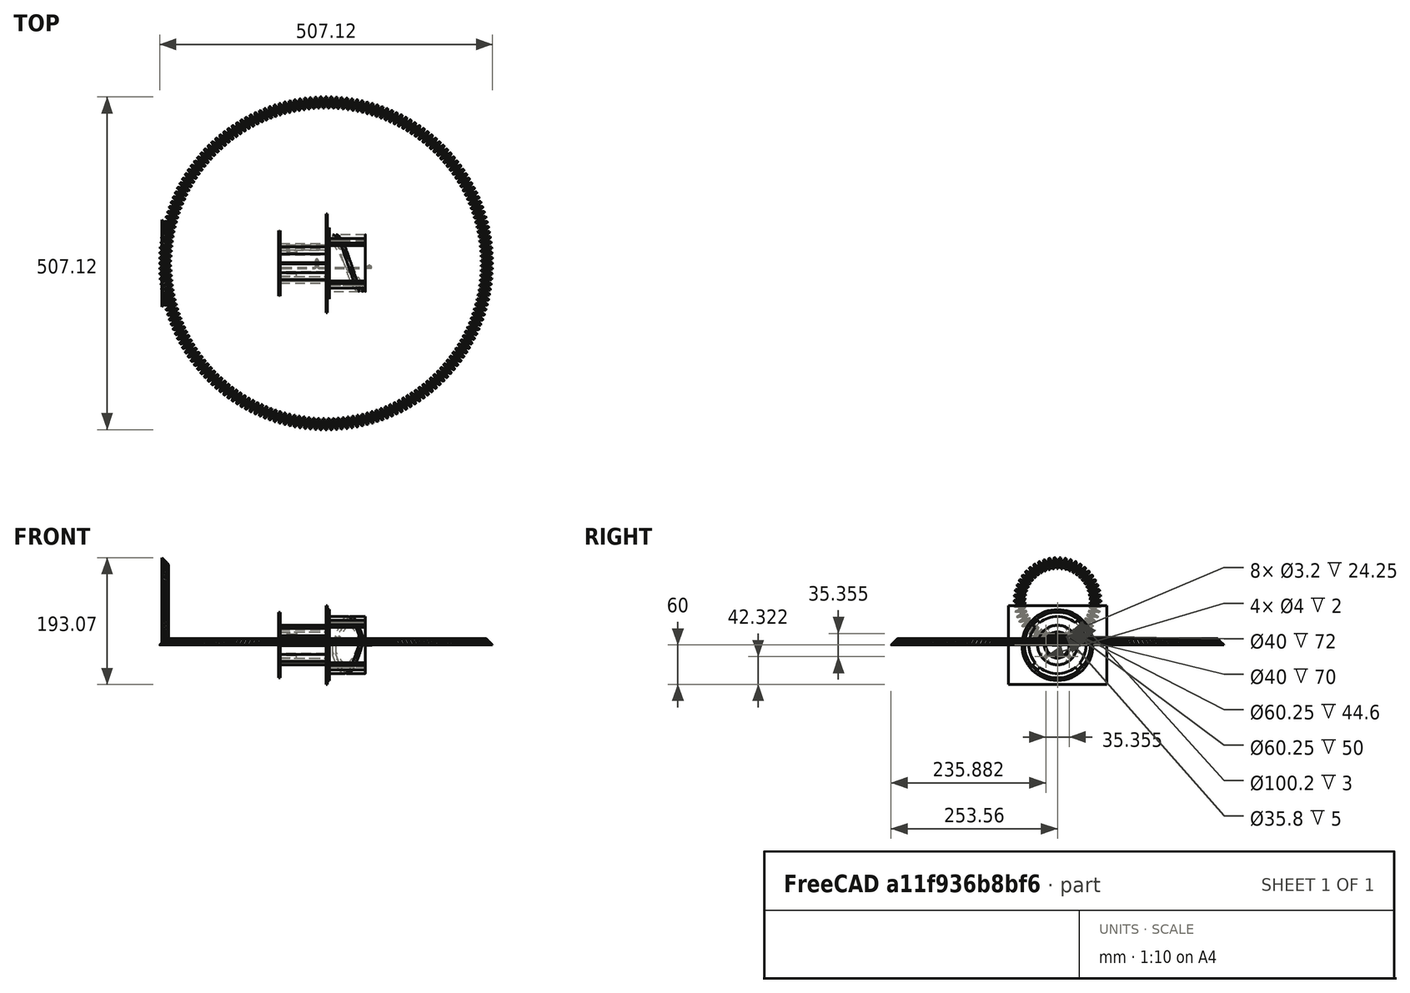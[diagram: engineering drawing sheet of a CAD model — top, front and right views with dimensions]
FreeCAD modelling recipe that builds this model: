
FCSTD DOCUMENT  (FreeCAD 1.0R38641 +468 (Git))
Label: knitting_machine
License: All rights reserved
LicenseURL: https://en.wikipedia.org/wiki/All_rights_reserved
objects: Sketcher::SketchObject×18, PartDesign::Pad×9, App::FeaturePython×6, PartDesign::Body×5, App::Link×5, App::Part×4, PartDesign::PolarPattern×3, Part::FeaturePython×3, PartDesign::AdditivePipe×2, PartDesign::AdditiveLoft×2, PartDesign::Pocket×2, PartDesign::SubtractiveHelix×2, PartDesign::Groove×2, Spreadsheet::Sheet×1, Image::ImagePlane×1, PartDesign::Chamfer×1, Assembly::JointGroup×1, Assembly::AssemblyObject×1
note: 110 computed .brp shape members not serialized (recipe doc carries the construction recipe); baked Part::Feature solids carry a one-line shape summary decoded from their .brp

FEATURE [Spreadsheet::Sheet] Spreadsheet  label="MasterSpreadsheet"
  cells = A2='hole_diameter; B2(hole_diameter)==40 mm; A3='needle_number; B3(needle_number)=12; A4='needle_length; B4(needle_length)==13.8 cm; A5='needle_thickness; B5(needle_thickness)==1.9 mm; A6='needle_width; B6(needle_width)==1.2 mm; A7='needle_knob_protrusion; B7(needle_knob_protrusion)==12.5 mm; A8='needle_know_height; B8(needle_knob_height)==needle_thickness * 2 + 0.1 mm; A9='travel_dist; B9(travel_dist)==40 mm; A10='travel_angle; B10(travel_angle)==160 °; A11='baseplate_diameter; B11(baseplate_diameter)==100 mm; A12='gear_module; B12(gear_module)=2; A13='gear_pressure_angle; B13(gear_pressure_angle)==20 °; A14='driven_Z; B14(driven_Z)=36; A15='driven_PCD; B15(driven_PCD)=72; A16='gear_Ck; B16(gear_Ck)==250 mm
FEATURE [Image::ImagePlane] needle_1  label="needle-1"
  XSize = 140
  YSize = 18.51
FEATURE [Sketcher::SketchObject] Sketch  label="Needle_profile"
  ArcFitTolerance = 1e-06
  AttachmentSupport = -> [XY_Plane001]
  FullyConstrained = true
  MakeInternals = false
  MapMode = 5
  expr: Constraints[19] = <<MasterSpreadsheet>>.needle_thickness + 0.1 mm
  expr: Constraints[29] = <<MasterSpreadsheet>>.needle_knob_protrusion
  sketch-geometry (11):
    g0: LineSegment StartX=-67 StartY=-7 StartZ=0 EndX=-18.2 EndY=-7 EndZ=0
    g1: LineSegment StartX=-15 StartY=-3.8 StartZ=0 EndX=-15 EndY=4.55 EndZ=0
    g2: LineSegment StartX=-13.95 StartY=5.5 StartZ=0 EndX=-14.05 EndY=5.5 EndZ=0
    g3: LineSegment StartX=-13 StartY=4.55 StartZ=0 EndX=-13 EndY=-3.8 EndZ=0
    g4: LineSegment StartX=-9.8 StartY=-7 StartZ=0 EndX=60 EndY=-7 EndZ=0
    g5: ArcOfCircle CenterX=-18.2 CenterY=-3.8 CenterZ=0 NormalX=0 NormalY=0 NormalZ=1 AngleXU=0 Radius=3.2 StartAngle=4.71239 EndAngle=6.28319
    g6: GeomPoint [constr] X=-15 Y=-7 Z=0
    g7: ArcOfCircle CenterX=-9.8 CenterY=-3.8 CenterZ=0 NormalX=0 NormalY=0 NormalZ=1 AngleXU=0 Radius=3.2 StartAngle=3.14159 EndAngle=4.71239
    g8: GeomPoint [constr] X=-13 Y=-7 Z=0
    g9: ArcOfCircle CenterX=-14.05 CenterY=4.55 CenterZ=0 NormalX=0 NormalY=0 NormalZ=1 AngleXU=0 Radius=0.95 StartAngle=1.5708 EndAngle=3.14159
    g10: ArcOfCircle CenterX=-13.95 CenterY=4.55 CenterZ=0 NormalX=0 NormalY=0 NormalZ=1 AngleXU=0 Radius=0.95 StartAngle=3e-16 EndAngle=1.5708
  constraints (30):
    c: Horizontal(g0)
    c: Vertical(g1)
    c: Vertical(g3)
    c: Horizontal(g4)
    c: Horizontal(g8,g6)
    c: Horizontal(g2)
    c: PointOnObject(g6,g0)
    c: PointOnObject(g6,g1)
    c: Tangent(g0,g5) = -1.5708
    c: Tangent(g1,g5) = -1.5708
    c: PointOnObject(g8,g3)
    c: PointOnObject(g8,g4)
    c: Tangent(g3,g7) = -1.5708
    c: Tangent(g4,g7) = -1.5708
    c: Equal(g5,g7)
    c: Distance(g0,g-1) = 7
    c: Distance(g0,g-2) = 67
    c: DistanceX(g-1,g4) = 60
    c: Distance(g3,g-2) = 13
    c: DistanceX(g1,g3) = 2
    c: Horizontal(g1,g3)
    c: Radius(g7) = 3.2
    c: Distance(g2,g2) = 0.1
    c: Coincident(g9,g1)
    c: Horizontal(g9,g1)
    c: Tangent(g9,g2) = -1.5708
    c: Coincident(g10,g3)
    c: Horizontal(g10,g3)
    c: Tangent(g10,g2) = -1.5708
    c: DistanceY(g4,g2) = 12.5
FEATURE [Sketcher::SketchObject] Sketch001  label="Needle_section"
  ArcFitTolerance = 1e-06
  AttachmentSupport = -> [YZ_Plane001]
  ExternalGeometry = -> [Sketch]
  FullyConstrained = true
  MakeInternals = false
  MapMode = 5
  Placement = pos=(0,0,0) rot=(0.57735,0.57735,0.57735;2.0944rad)
  expr: Constraints[26] = <<MasterSpreadsheet>>.needle_thickness
  expr: Constraints[27] = <<MasterSpreadsheet>>.needle_width
  sketch-geometry (13):
    g0: LineSegment StartX=-7.95 StartY=0.1 StartZ=0 EndX=-7.95 EndY=-0.1 EndZ=0
    g1: LineSegment StartX=-7.45 StartY=-0.6 StartZ=0 EndX=-6.55 EndY=-0.6 EndZ=0
    g2: LineSegment StartX=-6.05 StartY=-0.1 StartZ=0 EndX=-6.05 EndY=0.1 EndZ=0
    g3: LineSegment StartX=-6.55 StartY=0.6 StartZ=0 EndX=-7.45 EndY=0.6 EndZ=0
    g4: ArcOfCircle CenterX=-7.45 CenterY=0.1 CenterZ=0 NormalX=0 NormalY=0 NormalZ=1 AngleXU=0 Radius=0.5 StartAngle=1.5708 EndAngle=3.14159
    g5: ArcOfCircle CenterX=-7.45 CenterY=-0.1 CenterZ=0 NormalX=0 NormalY=0 NormalZ=1 AngleXU=0 Radius=0.5 StartAngle=3.14159 EndAngle=4.71239
    g6: ArcOfCircle CenterX=-6.55 CenterY=-0.1 CenterZ=0 NormalX=0 NormalY=0 NormalZ=1 AngleXU=0 Radius=0.5 StartAngle=4.71239 EndAngle=6.28319
    g7: ArcOfCircle CenterX=-6.55 CenterY=0.1 CenterZ=0 NormalX=0 NormalY=0 NormalZ=1 AngleXU=0 Radius=0.5 StartAngle=0 EndAngle=1.5708
    g8: GeomPoint [constr] X=-7.95 Y=0.6 Z=0
    g9: GeomPoint [constr] X=-6.05 Y=-0.6 Z=0
    g10: LineSegment [constr] StartX=-7.45 StartY=-0.1 StartZ=0 EndX=-6.55 EndY=0.1 EndZ=0
    g11: LineSegment [constr] StartX=-7.45 StartY=0.1 StartZ=0 EndX=-6.55 EndY=-0.1 EndZ=0
    g12: GeomPoint [constr] X=-7 Y=0 Z=0
  constraints (28):
    c: Tangent(g0,g4) = -1.5708
    c: Tangent(g0,g5) = -1.5708
    c: Tangent(g1,g5) = -1.5708
    c: Tangent(g1,g6) = -1.5708
    c: Tangent(g2,g6) = -1.5708
    c: Tangent(g2,g7) = -1.5708
    c: Tangent(g3,g7) = -1.5708
    c: Tangent(g3,g4) = -1.5708
    c: Vertical(g0)
    c: Vertical(g2)
    c: Horizontal(g1)
    c: Horizontal(g3)
    c: Equal(g4,g5)
    c: Equal(g5,g6)
    c: Equal(g6,g7)
    c: PointOnObject(g8,g0)
    c: PointOnObject(g8,g3)
    c: PointOnObject(g9,g1)
    c: PointOnObject(g9,g2)
    c: Radius(g5) = 0.5
    c: Coincident(g10,g5)
    c: Coincident(g10,g7)
    c: Coincident(g11,g4)
    c: Coincident(g11,g6)
    c: Symmetric(g10,g10,g12)
    c: Coincident(g12,g-3)
    c: DistanceX(g0,g2) = 1.9
    c: DistanceY(g1,g3) = 1.2
FEATURE [PartDesign::AdditivePipe] AdditivePipe
  AuxilleryCurvelinear = true
  AuxillerySpineTangent = false
  Binormal = (0,0,0)
  Mode = 0
  Placement = pos=(0,0,0) rot=(1,1,1;2.0944rad)
  Profile = -> Sketch001
  Refine = true
  Spine = -> Sketch
  SpineTangent = false
  Suppressed = false
  Transformation = 0
  Transition = 0
FEATURE [Sketcher::SketchObject] Sketch002
  ArcFitTolerance = 1e-06
  AttachmentSupport = -> [XY_Plane001]
  ExternalGeometry = -> [AdditivePipe]
  FullyConstrained = true
  MakeInternals = false
  MapMode = 5
  sketch-geometry (4):
    g0: GeomPoint X=60 Y=-7 Z=0
    g1: LineSegment StartX=60 StartY=-7 StartZ=0 EndX=68 EndY=-7 EndZ=0
    g2: ArcOfCircle CenterX=68 CenterY=-5.81584 CenterZ=0 NormalX=0 NormalY=0 NormalZ=1 AngleXU=0 Radius=1.18416 StartAngle=4.71239 EndAngle=7.73181
    g3: LineSegment StartX=68.1443 StartY=-4.6405 StartZ=0 EndX=67 EndY=-4.5 EndZ=0
  constraints (9):
    c: Symmetric(g-3,g-4,g0)
    c: Coincident(g1,g0)
    c: Horizontal(g1)
    c: Tangent(g2,g1) = -1.5708
    c: Tangent(g3,g2) = -1.5708
    c: DistanceX(g0,g3) = 7
    c: DistanceY(g0,g3) = 2.5
    c: Angle(g3,g-1) = 0.122173
    c: DistanceX(g0,g1) = 8
FEATURE [Sketcher::SketchObject] Sketch003
  ArcFitTolerance = 1e-06
  AttachmentSupport = -> [YZ_Plane001,Sketch002]
  ExternalGeometry = -> [Sketch002]
  FullyConstrained = true
  MakeInternals = false
  MapMode = 53
  Placement = pos=(68,-7.5e-15,7.5e-15) rot=(0.57735,0.57735,0.57735;2.0944rad)
  expr: Constraints[1] = <<MasterSpreadsheet>>.needle_width
  sketch-geometry (1):
    g0: Circle CenterX=-7 CenterY=0 CenterZ=0 NormalX=0 NormalY=0 NormalZ=1 AngleXU=0 Radius=0.6
  constraints (2):
    c: Coincident(g0,g-3)
    c: Diameter(g0) = 1.2
FEATURE [Sketcher::SketchObject] Sketch004
  ArcFitTolerance = 1e-06
  AttachmentSupport = -> [Sketch002]
  FullyConstrained = true
  MakeInternals = false
  MapMode = 1
  Placement = pos=(67,-4.5,0) rot=(0.624332,0.552363,0.552363;2.02535rad)
  sketch-geometry (1):
    g0: Circle CenterX=0 CenterY=0 CenterZ=0 NormalX=0 NormalY=0 NormalZ=1 AngleXU=0 Radius=0.15
  constraints (2):
    c: Diameter(g0) = 0.3
    c: Coincident(g0,g-1)
FEATURE [PartDesign::AdditiveLoft] AdditiveLoft
  BaseFeature = -> AdditivePipe
  Closed = false
  Placement = pos=(0,0,0) rot=(1,1,1;2.0944rad)
  Profile = -> AdditivePipe [Face49]
  Refine = true
  Ruled = false
  Sections = -> [Sketch003]
  Suppressed = false
FEATURE [Sketcher::SketchObject] Sketch005
  ArcFitTolerance = 1e-06
  AttachmentSupport = -> [Sketch002]
  FullyConstrained = true
  MakeInternals = false
  MapMode = 7
  Placement = pos=(68.1443,-4.6405,0) rot=(0.624332,0.552363,0.552363;2.02535rad)
  sketch-geometry (1):
    g0: Circle CenterX=0 CenterY=0 CenterZ=0 NormalX=0 NormalY=0 NormalZ=1 AngleXU=0 Radius=0.2
  constraints (2):
    c: Diameter(g0) = 0.4
    c: Coincident(g0,g-1)
FEATURE [PartDesign::AdditivePipe] AdditivePipe001
  AuxilleryCurvelinear = true
  AuxillerySpineTangent = false
  BaseFeature = -> AdditiveLoft
  Binormal = (0,0,0)
  Mode = 0
  Placement = pos=(0,0,0) rot=(1,1,1;2.0944rad)
  Profile = -> AdditiveLoft [Face55]
  Refine = true
  Sections = -> [Sketch005]
  Spine = -> Sketch002 [Edge2]
  SpineTangent = false
  Suppressed = false
  Transformation = 1
  Transition = 0
FEATURE [PartDesign::AdditiveLoft] AdditiveLoft001
  BaseFeature = -> AdditivePipe001
  Closed = false
  Placement = pos=(0,0,0) rot=(1,1,1;2.0944rad)
  Profile = -> AdditivePipe001 [Face68]
  Refine = true
  Ruled = false
  Sections = -> [Sketch004]
  Suppressed = false
FEATURE [Sketcher::SketchObject] Sketch006
  ArcFitTolerance = 1e-06
  AttachmentSupport = -> [AdditiveLoft001]
  ExternalGeometry = -> [AdditiveLoft001]
  FullyConstrained = true
  MakeInternals = false
  MapMode = 5
  Placement = pos=(0,-6.05,6.7e-15) rot=(0.57735,0.57735,0.57735;4.18879rad)
  sketch-geometry (5):
    g0: LineSegment StartX=-0.2 StartY=59.8 StartZ=0 EndX=0.2 EndY=59.8 EndZ=0
    g1: LineSegment StartX=0.2 StartY=59.8 StartZ=0 EndX=0.2 EndY=61.8 EndZ=0
    g2: LineSegment StartX=0.2 StartY=61.8 StartZ=0 EndX=-0.2 EndY=61.8 EndZ=0
    g3: LineSegment StartX=-0.2 StartY=61.8 StartZ=0 EndX=-0.2 EndY=59.8 EndZ=0
    g4: GeomPoint [constr] X=0 Y=60.8 Z=0
  constraints (13):
    c: Coincident(g0,g1)
    c: Coincident(g1,g2)
    c: Coincident(g2,g3)
    c: Coincident(g3,g0)
    c: Horizontal(g0)
    c: Horizontal(g2)
    c: Vertical(g1)
    c: Vertical(g3)
    c: Symmetric(g2,g0,g4)
    c: PointOnObject(g4,g-2)
    c: DistanceY(g1,g1) = 2
    c: Distance(g2,g2) = 0.4
    c: Distance(g-3,g0) = 0.2
FEATURE [PartDesign::Pad] Pad
  BaseFeature = -> AdditiveLoft001
  Direction = (-1e-16,1,-1e-15)
  Length = 0.3
  Length2 = 10
  Placement = pos=(0,0,0) rot=(1,1,1;2.0944rad)
  Profile = -> Sketch006
  ReferenceAxis = -> Sketch006 [N_Axis]
  Refine = true
  Reversed = true
  Suppressed = false
  Type = 0
FEATURE [Sketcher::SketchObject] Sketch007
  ArcFitTolerance = 1e-06
  AttachmentSupport = -> [Pad]
  ExternalGeometry = -> [Pad]
  FullyConstrained = true
  MakeInternals = false
  MapMode = 5
  Placement = pos=(-1e-16,3e-16,0.2) rot=(0,0,-1;1.5708rad)
  sketch-geometry (6):
    g0: LineSegment StartX=6.05 StartY=59.8 StartZ=0 EndX=3.01351 EndY=65.3199 EndZ=0
    g1: LineSegment StartX=6.05 StartY=59.8 StartZ=0 EndX=6.05 EndY=61.8 EndZ=0
    g2: LineSegment StartX=6.05 StartY=61.8 StartZ=0 EndX=3.18212 EndY=65.8958 EndZ=0
    g3: ArcOfCircle CenterX=4.76587 CenterY=66.2839 CenterZ=0 NormalX=0 NormalY=0 NormalZ=1 AngleXU=0 Radius=2 StartAngle=2.9064 EndAngle=3.64451
    g4: ArcOfCircle CenterX=3.01542 CenterY=66.7034 CenterZ=0 NormalX=0 NormalY=0 NormalZ=1 AngleXU=0 Radius=0.2 StartAngle=6.24175 EndAngle=9.18959
    g5: LineSegment StartX=3.18212 StartY=65.8958 StartZ=0 EndX=3.21525 EndY=66.6951 EndZ=0
  constraints (15):
    c: Coincident(g-3,g0)
    c: Coincident(g0,g1)
    c: Coincident(g1,g-3)
    c: Coincident(g1,g2)
    c: Coincident(g5,g2)
    c: Tangent(g5,g4) = -1.5708
    c: Tangent(g3,g0) = 1.5708
    c: Tangent(g4,g3) = -1.5708
    c: Radius(g4) = 0.2
    c: Radius(g3) = 2
    c: Distance(g0,g2) = 0.6
    c: Distance(g2,g2) = 5
    c: Distance(g0,g0) = 6.3
    c: Distance(g5,g5) = 0.8
    c: Angle(g-2,g2) = 0.610865
FEATURE [PartDesign::Pad] Pad001
  BaseFeature = -> Pad
  Direction = (0,1.3e-15,1)
  Length = 10
  Length2 = 10
  Placement = pos=(0,0,0) rot=(1,1,1;2.0944rad)
  Profile = -> Sketch007
  ReferenceAxis = -> Sketch007 [N_Axis]
  Refine = true
  Reversed = true
  Suppressed = false
  Type = 3
  UpToFace = -> Pad [Face54]
FEATURE [PartDesign::Body] Body  label="Body_needle"
  AllowCompound = false
  Group = -> [Sketch,Sketch001,AdditivePipe,Sketch002,Sketch003,Sketch004,AdditiveLoft,Sketch005,AdditivePipe001,AdditiveLoft001,Sketch006,Pad,Sketch007,Pad001]
  Origin = -> Origin001
  Tip = -> Pad001
FEATURE [App::Part] Part  label="Needle"
  Group = -> [Body,needle_1]
  Origin = -> Origin
  Placement = pos=(-44,35.5,0) rot=(0,0,1;0rad)
FEATURE [Sketcher::SketchObject] Sketch008
  ArcFitTolerance = 1e-06
  AttachmentSupport = -> [YZ_Plane003]
  FullyConstrained = true
  MakeInternals = false
  MapMode = 5
  Placement = pos=(0,0,0) rot=(0.57735,0.57735,0.57735;2.0944rad)
  expr: Constraints[2] = <<MasterSpreadsheet>>.hole_diameter
  sketch-geometry (2):
    g0: Circle CenterX=0 CenterY=0 CenterZ=0 NormalX=0 NormalY=0 NormalZ=1 AngleXU=0 Radius=20
    g1: Circle CenterX=0 CenterY=0 CenterZ=0 NormalX=0 NormalY=0 NormalZ=1 AngleXU=0 Radius=30
  constraints (4):
    c: Coincident(g0,g-1)
    c: Coincident(g1,g0)
    c: Diameter(g0) = 40
    c: Distance(g1,g0) = 10
FEATURE [PartDesign::Pad] Pad002
  Direction = (1,0,0)
  Length = 70
  Length2 = 10
  Placement = pos=(0,0,0) rot=(1,1,1;2.0944rad)
  Profile = -> Sketch008
  ReferenceAxis = -> Sketch008 [N_Axis]
  Refine = true
  Reversed = true
  Suppressed = false
  Type = 0
FEATURE [Sketcher::SketchObject] Sketch009
  ArcFitTolerance = 1e-06
  AttachmentSupport = -> [Pad002]
  ExternalGeometry = -> [Pad002]
  FullyConstrained = true
  MakeInternals = false
  MapMode = 5
  Placement = pos=(0,0,0) rot=(0.57735,0.57735,0.57735;2.0944rad)
  expr: Constraints[17] = <<MasterSpreadsheet>>.needle_thickness
  expr: Constraints[18] = <<MasterSpreadsheet>>.needle_width + 0.2 mm
  sketch-geometry (8):
    g0: ArcOfCircle CenterX=29.573 CenterY=1.26471 CenterZ=0 NormalX=0 NormalY=0 NormalZ=1 AngleXU=0 Radius=0.4 StartAngle=4.79966 EndAngle=6.32592
    g1: ArcOfCircle CenterX=27.7078 CenterY=0 CenterZ=0 NormalX=0 NormalY=0 NormalZ=1 AngleXU=0 Radius=0.7 StartAngle=1.5708 EndAngle=4.71239
    g2: ArcOfCircle CenterX=29.573 CenterY=-1.26471 CenterZ=0 NormalX=0 NormalY=0 NormalZ=1 AngleXU=0 Radius=0.4 StartAngle=6.24045 EndAngle=7.76672
    g3: ArcOfCircle CenterX=0 CenterY=0 CenterZ=0 NormalX=0 NormalY=0 NormalZ=1 AngleXU=0 Radius=30 StartAngle=6.24045 EndAngle=6.32592
    g4: LineSegment StartX=27.7078 StartY=0.7 StartZ=0 EndX=29.6078 EndY=0.866228 EndZ=0
    g5: LineSegment StartX=29.6078 StartY=-0.866228 StartZ=0 EndX=27.7078 EndY=-0.7 EndZ=0
    g6: LineSegment [constr] StartX=29.6078 StartY=0.866228 StartZ=0 EndX=29.6078 EndY=-0.866228 EndZ=0
    g7: GeomPoint [constr] X=29.6078 Y=0 Z=0
  constraints (21):
    c: PointOnObject(g0,g-3)
    c: PointOnObject(g1,g-1)
    c: Equal(g2,g0)
    c: Coincident(g3,g-1)
    c: Coincident(g5,g1)
    c: Tangent(g3,g2) = -1.5708
    c: Tangent(g3,g0) = -1.5708
    c: Coincident(g4,g1)
    c: Vertical(g1,g1)
    c: Vertical(g1,g1)
    c: Coincident(g0,g4)
    c: Coincident(g6,g0)
    c: Coincident(g6,g2)
    c: Vertical(g6)
    c: Symmetric(g6,g6,g7)
    c: PointOnObject(g7,g-1)
    c: Radius(g0) = 0.4
    c: DistanceX(g1,g7) = 1.9
    c: DistanceY(g1,g1) = 1.4
    c: Angle(g-1,g4) = 0.0872665
    c: Tangent(g5,g2) = -1.5708
FEATURE [PartDesign::Pocket] Pocket
  BaseFeature = -> Pad002
  Direction = (-1,0,0)
  Length = 5
  Length2 = 5
  Placement = pos=(0,0,0) rot=(1,1,1;2.0944rad)
  Profile = -> Sketch009
  ReferenceAxis = -> Sketch009 [N_Axis]
  Refine = true
  Suppressed = false
  Type = 2
FEATURE [PartDesign::PolarPattern] PolarPattern
  Angle = 360
  Axis = -> Sketch009 [N_Axis]
  BaseFeature = -> Pocket
  Mode = 0
  Occurrences = 12
  Offset = 120
  Originals = -> [Pocket]
  Placement = pos=(0,0,0) rot=(1,1,1;2.0944rad)
  Refine = true
  Suppressed = false
  TransformMode = 0
  expr: Occurrences = <<MasterSpreadsheet>>.needle_number
FEATURE [Sketcher::SketchObject] Sketch012
  ArcFitTolerance = 1e-06
  AttachmentSupport = -> [YZ_Plane005]
  FullyConstrained = true
  MakeInternals = false
  MapMode = 5
  Placement = pos=(0,0,0) rot=(0.57735,0.57735,0.57735;2.0944rad)
  expr: Constraints[13] = <<MasterSpreadsheet>>.hole_diameter - 0.2 mm
  sketch-geometry (6):
    g0: LineSegment StartX=-75 StartY=60 StartZ=0 EndX=-75 EndY=-60 EndZ=0
    g1: LineSegment StartX=-75 StartY=-60 StartZ=0 EndX=75 EndY=-60 EndZ=0
    g2: LineSegment StartX=75 StartY=-60 StartZ=0 EndX=75 EndY=60 EndZ=0
    g3: LineSegment StartX=75 StartY=60 StartZ=0 EndX=-75 EndY=60 EndZ=0
    g4: GeomPoint [constr] X=0 Y=0 Z=0
    g5: Circle CenterX=0 CenterY=0 CenterZ=0 NormalX=0 NormalY=0 NormalZ=1 AngleXU=0 Radius=19.9
  constraints (14):
    c: Coincident(g0,g1)
    c: Coincident(g1,g2)
    c: Coincident(g2,g3)
    c: Coincident(g3,g0)
    c: Vertical(g0)
    c: Vertical(g2)
    c: Horizontal(g1)
    c: Horizontal(g3)
    c: Symmetric(g2,g0,g4)
    c: Coincident(g4,g-1)
    c: Coincident(g5,g4)
    c: DistanceX(g1,g1) = 150
    c: DistanceY(g0,g0) = 120
    c: Diameter(g5) = 39.8
FEATURE [PartDesign::Pad] Pad004
  Direction = (1,0,0)
  Length = 2
  Length2 = 10
  Placement = pos=(0,0,0) rot=(1,1,1;2.0944rad)
  Profile = -> Sketch012
  ReferenceAxis = -> Sketch012 [N_Axis]
  Refine = true
  Suppressed = false
  Type = 0
FEATURE [Sketcher::SketchObject] Sketch013
  ArcFitTolerance = 1e-06
  AttachmentSupport = -> [YZ_Plane005]
  ExternalGeometry = -> [Pad004]
  FullyConstrained = true
  MakeInternals = false
  MapMode = 5
  Placement = pos=(0,0,0) rot=(0.57735,0.57735,0.57735;2.0944rad)
  sketch-geometry (2):
    g0: Circle CenterX=0 CenterY=0 CenterZ=0 NormalX=0 NormalY=0 NormalZ=1 AngleXU=0 Radius=19.9
    g1: Circle CenterX=0 CenterY=0 CenterZ=0 NormalX=0 NormalY=0 NormalZ=1 AngleXU=0 Radius=17.9
  constraints (4):
    c: Coincident(g0,g-1)
    c: Equal(g-3,g0)
    c: Coincident(g1,g0)
    c: Distance(g1,g0) = 2
FEATURE [PartDesign::Pad] Pad005
  BaseFeature = -> Pad004
  Direction = (1,0,0)
  Length = 5
  Length2 = 10
  Offset = 1
  Placement = pos=(0,0,0) rot=(1,1,1;2.0944rad)
  Profile = -> Sketch013
  ReferenceAxis = -> Sketch013 [N_Axis]
  Refine = true
  Suppressed = false
  Type = 0
FEATURE [Sketcher::SketchObject] Sketch014
  ArcFitTolerance = 1e-06
  AttachmentSupport = -> [YZ_Plane005]
  FullyConstrained = true
  MakeInternals = false
  MapMode = 5
  Placement = pos=(0,0,0) rot=(0.57735,0.57735,0.57735;2.0944rad)
  sketch-geometry (2):
    g0: Circle CenterX=0 CenterY=0 CenterZ=0 NormalX=0 NormalY=0 NormalZ=1 AngleXU=0 Radius=50.1
    g1: Circle CenterX=0 CenterY=0 CenterZ=0 NormalX=0 NormalY=0 NormalZ=1 AngleXU=0 Radius=54.1
  constraints (4):
    c: Coincident(g0,g-1)
    c: Coincident(g1,g0)
    c: Diameter(g0) = 100.2
    c: Distance(g0,g1) = 4
FEATURE [PartDesign::Pad] Pad006
  BaseFeature = -> Pad005
  Direction = (1,0,0)
  Length = 10
  Length2 = 10
  Placement = pos=(0,0,0) rot=(1,1,1;2.0944rad)
  Profile = -> Sketch014
  ReferenceAxis = -> Sketch014 [N_Axis]
  Refine = true
  Suppressed = false
  Type = 3
  UpToFace = -> Pad005 [Face7]
FEATURE [PartDesign::Body] Body002  label="Body_baseplate"
  AllowCompound = false
  Group = -> [Sketch012,Pad004,Sketch013,Pad005,Sketch014,Pad006]
  Origin = -> Origin005
  Tip = -> Pad006
FEATURE [App::Part] Part002  label="Baseplate"
  Group = -> [Body002]
  Origin = -> Origin004
  Placement = pos=(-74,0,0) rot=(0,0,1;0rad)
FEATURE [App::Link] Baseplate  label="Baseplate001"
  LinkedObject = -> Part002
FEATURE [App::FeaturePython] GroundedJoint  # Assembly grounded joint (typed FeaturePython)
  ObjectToGround = -> Baseplate
FEATURE [Part::FeaturePython] BevelGear  label="DrivenGear"  # WARN: FeaturePython — macro-defined, semantics opaque (R4)
  AttacherType = Attacher::AttachEngine3D
  angular_backlash = 0
  backlash = 0
  beta = 0
  clearance = 0.1
  dw = 500
  height = 10
  module = 2.5
  num_teeth = 200
  numpoints = 20
  pitch_angle = 45
  pressure_angle = 20
  reset_origin = true
  version = 1.3.0
  expr: angular_backlash = backlash / dw * 360 ° / pi
  expr: dw = num_teeth * module
FEATURE [Part::FeaturePython] BevelGear001  label="DriverGear"  # WARN: FeaturePython — macro-defined, semantics opaque (R4)
  AttacherType = Attacher::AttachEngine3D
  Placement = pos=(-250,0,67) rot=(0,1,0;1.5708rad)
  angular_backlash = 0
  backlash = 0
  beta = 0
  clearance = 0.1
  dw = 125
  height = 10
  module = 2.5
  num_teeth = 50
  numpoints = 20
  pitch_angle = 45
  pressure_angle = 20
  reset_origin = true
  version = 1.3.0
  expr: angular_backlash = backlash / dw * 360 ° / pi
  expr: dw = num_teeth * module
FEATURE [Part::FeaturePython] GearConnector  # WARN: FeaturePython — macro-defined, semantics opaque (R4)
  angle1 = 0
  angle2 = 0
  master_gear = -> BevelGear001
  slave_gear = -> BevelGear
  version = 1.3.0
FEATURE [App::Link] Needle  label="Needle001"
  LinkPlacement = pos=(53.4292,34.6278,8.51578) rot=(1,0,0;0.231323rad)
  LinkedObject = -> Part
  Placement = pos=(53.4292,34.6278,8.51578) rot=(1,0,0;0.231323rad)
FEATURE [App::Link] Needle001  label="Needle002"
  LinkPlacement = pos=(71.2601,-34.2464,9.93902) rot=(1,0,0;2.84932rad)
  LinkedObject = -> Part
  Placement = pos=(71.2601,-34.2464,9.93902) rot=(1,0,0;2.84932rad)
FEATURE [Sketcher::SketchObject] Sketch015
  ArcFitTolerance = 1e-06
  AttachmentSupport = -> [YZ_Plane008]
  FullyConstrained = true
  MakeInternals = false
  MapMode = 5
  Placement = pos=(0,0,0) rot=(0.57735,0.57735,0.57735;2.0944rad)
  expr: Constraints[3] = 60 mm + 2 mm + 2 * <<MasterSpreadsheet>>.needle_knob_protrusion
  sketch-geometry (2):
    g0: Circle CenterX=0 CenterY=0 CenterZ=0 NormalX=0 NormalY=0 NormalZ=1 AngleXU=0 Radius=30.125
    g1: Circle CenterX=0 CenterY=0 CenterZ=0 NormalX=0 NormalY=0 NormalZ=1 AngleXU=0 Radius=43.5
  constraints (4):
    c: Coincident(g0,g-1)
    c: Coincident(g1,g0)
    c: Diameter(g0) = 60.25
    c: Diameter(g1) = 87
FEATURE [PartDesign::Pad] Pad007
  Direction = (1,0,0)
  Length = 60
  Length2 = 10
  Placement = pos=(0,0,0) rot=(1,1,1;2.0944rad)
  Profile = -> Sketch015
  ReferenceAxis = -> Sketch015 [N_Axis]
  Refine = true
  Suppressed = false
  Type = 0
  expr: Length = <<MasterSpreadsheet>>.travel_dist + 20 mm
FEATURE [Sketcher::SketchObject] Sketch017
  ArcFitTolerance = 1e-06
  AttachmentSupport = -> [Pad007]
  ExternalGeometry = -> [Pad007]
  FullyConstrained = true
  MakeInternals = false
  MapMode = 5
  Placement = pos=(60,-1.33e-14,6.7e-15) rot=(0.57735,0.57735,0.57735;2.0944rad)
  sketch-geometry (6):
    g0: LineSegment StartX=-34.0908 StartY=27.0197 StartZ=0 EndX=-27.0197 EndY=34.0908 EndZ=0
    g1: LineSegment StartX=-34.0908 StartY=27.0197 StartZ=0 EndX=-37.6263 EndY=30.5553 EndZ=0
    g2: LineSegment StartX=-37.6263 StartY=30.5553 StartZ=0 EndX=-30.5553 EndY=37.6263 EndZ=0
    g3: LineSegment StartX=-30.5553 StartY=37.6263 StartZ=0 EndX=-27.0197 EndY=34.0908 EndZ=0
    g4: GeomPoint X=-30.5553 Y=30.5553 Z=0
    g5: LineSegment [constr] StartX=0 StartY=0 StartZ=0 EndX=-30.5553 EndY=30.5553 EndZ=0
  constraints (15):
    c: PointOnObject(g0,g-3)
    c: PointOnObject(g0,g-3)
    c: Coincident(g0,g1)
    c: Coincident(g1,g2)
    c: Coincident(g2,g3)
    c: Coincident(g3,g0)
    c: Perpendicular(g2,g3)
    c: Perpendicular(g2,g1)
    c: Perpendicular(g0,g1)
    c: Distance(g1,g1) = 5
    c: Distance(g2,g2) = 10
    c: Symmetric(g0,g0,g4)
    c: Coincident(g5,g-1)
    c: Coincident(g5,g4)
    c: Angle(g-2,g5) = 0.785398
FEATURE [PartDesign::Pad] Pad008
  BaseFeature = -> Pad007
  Direction = (1,0,0)
  Length = 8
  Length2 = 10
  Placement = pos=(0,0,0) rot=(1,1,1;2.0944rad)
  Profile = -> Sketch017
  ReferenceAxis = -> Sketch017 [N_Axis]
  Refine = true
  Reversed = true
  Suppressed = false
  Type = 3
  UpToFace = -> Pad007 [Face3]
FEATURE [PartDesign::PolarPattern] PolarPattern001
  Angle = 360
  Axis = -> Sketch015 [N_Axis]
  BaseFeature = -> Pad008
  Mode = 0
  Occurrences = 4
  Offset = 120
  Originals = -> [Pad008]
  Placement = pos=(0,0,0) rot=(1,1,1;2.0944rad)
  Refine = true
  Suppressed = false
  TransformMode = 0
FEATURE [Sketcher::SketchObject] Sketch018
  ArcFitTolerance = 1e-06
  AttachmentSupport = -> [XY_Plane008]
  ExternalGeometry = -> [PolarPattern001]
  FullyConstrained = true
  MakeInternals = false
  MapMode = 5
  expr: Constraints[14] = <<MasterSpreadsheet>>.needle_knob_height + 1.5 mm
  sketch-geometry (6):
    g0: LineSegment [constr] StartX=0 StartY=43.5 StartZ=0 EndX=60 EndY=43.5 EndZ=0
    g1: LineSegment [constr] StartX=60 StartY=30.125 StartZ=0 EndX=0 EndY=30.125 EndZ=0
    g2: LineSegment StartX=10 StartY=43.5 StartZ=0 EndX=10 EndY=30.125 EndZ=0
    g3: LineSegment StartX=10 StartY=30.125 StartZ=0 EndX=15.4 EndY=30.125 EndZ=0
    g4: LineSegment StartX=15.4 StartY=30.125 StartZ=0 EndX=15.4 EndY=43.5 EndZ=0
    g5: LineSegment StartX=15.4 StartY=43.5 StartZ=0 EndX=10 EndY=43.5 EndZ=0
  constraints (16):
    c: Coincident(g0,g-4)
    c: Coincident(g0,g-6)
    c: Coincident(g1,g-5)
    c: Coincident(g1,g-3)
    c: Coincident(g2,g3)
    c: Coincident(g3,g4)
    c: Coincident(g4,g5)
    c: Coincident(g5,g2)
    c: Vertical(g2)
    c: Vertical(g4)
    c: Horizontal(g3)
    c: Horizontal(g5)
    c: PointOnObject(g2,g0)
    c: PointOnObject(g3,g1)
    c: DistanceX(g5,g5) = 5.4
    c: DistanceX(g0,g2) = 10
FEATURE [PartDesign::SubtractiveHelix] SubtractiveHelix
  Angle = 0
  Axis = (1,0,0)
  Base = (0,0,0)
  BaseFeature = -> PolarPattern001
  Growth = 0
  HasBeenEdited = true
  Height = 40
  LeftHanded = false
  Mode = 2
  Outside = false
  Pitch = 90
  Placement = pos=(0,0,0) rot=(1,1,1;2.0944rad)
  Profile = -> Sketch018
  ReferenceAxis = -> X_Axis008
  Refine = true
  Suppressed = false
  Tolerance = 0.1
  Turns = 0.444444
  expr: Height = <<MasterSpreadsheet>>.travel_dist
  expr: Turns = <<MasterSpreadsheet>>.travel_angle / 360 °
FEATURE [PartDesign::Groove] Groove
  Angle = 20
  Angle2 = 60
  Axis = (1,0,0)
  Base = (0,0,0)
  BaseFeature = -> SubtractiveHelix
  Placement = pos=(0,0,0) rot=(1,1,1;2.0944rad)
  Profile = -> SubtractiveHelix [Face22]
  ReferenceAxis = -> X_Axis008
  Refine = true
  Suppressed = false
  Type = 0
  expr: Angle = 180 ° - <<MasterSpreadsheet>>.travel_angle
FEATURE [PartDesign::SubtractiveHelix] SubtractiveHelix001
  Angle = 0
  Axis = (1,0,0)
  Base = (0,0,0)
  BaseFeature = -> Groove
  Growth = 0
  HasBeenEdited = true
  Height = 40
  LeftHanded = true
  Mode = 2
  Outside = false
  Pitch = 90
  Placement = pos=(0,0,0) rot=(1,1,1;2.0944rad)
  Profile = -> Groove [Face23]
  ReferenceAxis = -> X_Axis008
  Refine = true
  Reversed = true
  Suppressed = false
  Tolerance = 0.1
  Turns = 0.444444
  expr: Height = <<MasterSpreadsheet>>.travel_dist
  expr: Turns = <<MasterSpreadsheet>>.travel_angle / 360 °
FEATURE [PartDesign::Groove] Groove001
  Angle = 20
  Angle2 = 60
  Axis = (1,0,0)
  Base = (0,0,0)
  BaseFeature = -> SubtractiveHelix001
  Placement = pos=(0,0,0) rot=(1,1,1;2.0944rad)
  Profile = -> SubtractiveHelix001 [Face15]
  ReferenceAxis = -> X_Axis008
  Refine = true
  Suppressed = false
  Type = 0
  expr: Angle = 180 ° - <<MasterSpreadsheet>>.travel_angle
FEATURE [PartDesign::Body] Body003  label="BotTrack"
  AllowCompound = false
  Group = -> [Sketch015,Pad007,Sketch017,Pad008,PolarPattern001,Sketch018,SubtractiveHelix,Groove,SubtractiveHelix001,Groove001]
  Origin = -> Origin008
  Tip = -> Groove001
FEATURE [App::Part] Part003  label="track"
  Group = -> [Body003]
  Origin = -> Origin007
FEATURE [App::Link] track  label="track001"
  LinkPlacement = pos=(5,0,1.7e-15) rot=(0,0,1;0rad)
  LinkedObject = -> Part003
  Placement = pos=(5,0,1.7e-15) rot=(0,0,1;0rad)
FEATURE [App::FeaturePython] Joint003  label="Fixed"  # Assembly joint (typed FeaturePython)
  Activated = true
  AngleMax = 0
  AngleMin = 0
  Detach1 = false
  Detach2 = false
  Distance = 0
  Distance2 = 0
  EnableAngleMax = false
  EnableAngleMin = false
  EnableLengthMax = false
  EnableLengthMin = false
  JointType = 0 (Fixed)
  LengthMax = 0
  LengthMin = 0
  Placement2 = pos=(5,0,1.7e-15) rot=(0.57735,0.57735,-0.57735;4.18879rad)
  Reference1 = -> Assembly [track.Body003.?Edge94,track.Body003.?Edge94]
  Reference2 = -> Assembly [Baseplate.Body002.Edge16,Baseplate.Body002.Edge16]
FEATURE [Sketcher::SketchObject] Sketch019
  ArcFitTolerance = 1e-06
  AttachmentSupport = -> [PolarPattern]
  ExternalGeometry = -> [PolarPattern]
  FullyConstrained = true
  MakeInternals = false
  MapMode = 5
  Placement = pos=(-70,3.11e-14,-1.55e-14) rot=(0.57735,0.57735,-0.57735;4.18879rad)
  sketch-geometry (2):
    g0: Circle CenterX=17.6777 CenterY=-17.6777 CenterZ=0 NormalX=0 NormalY=0 NormalZ=1 AngleXU=0 Radius=1.6
    g1: LineSegment [constr] StartX=0 StartY=0 StartZ=0 EndX=17.6777 EndY=-17.6777 EndZ=0
  constraints (5):
    c: Coincident(g1,g-1)
    c: Coincident(g1,g0)
    c: Angle(g1,g-1) = 0.785398
    c: Diameter(g0) = 3.2
    c: Distance(g0,g-3) = 5
FEATURE [PartDesign::Pocket] Pocket001
  BaseFeature = -> PolarPattern
  Direction = (1,0,0)
  Length = 25
  Length2 = 5
  Placement = pos=(0,0,0) rot=(1,1,1;2.0944rad)
  Profile = -> Sketch019
  ReferenceAxis = -> Sketch019 [N_Axis]
  Refine = true
  Suppressed = false
  Type = 0
FEATURE [PartDesign::PolarPattern] PolarPattern002
  Angle = 360
  Axis = -> Sketch019 [N_Axis]
  BaseFeature = -> Pocket001
  Mode = 0
  Occurrences = 4
  Offset = 120
  Originals = -> [Pocket001]
  Placement = pos=(0,0,0) rot=(1,1,1;2.0944rad)
  Refine = true
  Suppressed = false
  TransformMode = 0
FEATURE [PartDesign::Chamfer] Chamfer
  Angle = 45
  Base = -> PolarPattern002 [Edge149,Edge151,Edge153,Edge150]
  BaseFeature = -> PolarPattern002
  ChamferType = 0
  FlipDirection = false
  Placement = pos=(0,0,0) rot=(1,1,1;2.0944rad)
  Refine = true
  Size = 0.75
  Size2 = 1
  SupportTransform = false
  Suppressed = false
  UseAllEdges = false
FEATURE [PartDesign::Body] Body001  label="needleguide001"
  AllowCompound = false
  Group = -> [Sketch008,Pad002,Sketch009,Pocket,PolarPattern,Sketch019,Pocket001,PolarPattern002,Chamfer]
  Origin = -> Origin003
  Tip = -> Chamfer
FEATURE [Sketcher::SketchObject] Sketch020
  ArcFitTolerance = 1e-06
  AttachmentSupport = -> [Chamfer]
  FullyConstrained = true
  MakeInternals = false
  MapMode = 5
  Placement = pos=(-70,4.66e-14,-2.33e-14) rot=(0.57735,0.57735,-0.57735;4.18879rad)
  expr: Constraints[2] = <<MasterSpreadsheet>>.hole_diameter
  expr: Constraints[3] = <<MasterSpreadsheet>>.baseplate_diameter
  sketch-geometry (10):
    g0: Circle CenterX=0 CenterY=0 CenterZ=0 NormalX=0 NormalY=0 NormalZ=1 AngleXU=0 Radius=20
    g1: Circle CenterX=0 CenterY=0 CenterZ=0 NormalX=0 NormalY=0 NormalZ=1 AngleXU=0 Radius=50
    g2: Circle CenterX=17.6777 CenterY=17.6777 CenterZ=0 NormalX=0 NormalY=0 NormalZ=1 AngleXU=0 Radius=2
    g3: LineSegment [constr] StartX=0 StartY=0 StartZ=0 EndX=17.6777 EndY=17.6777 EndZ=0
    g4: Circle CenterX=-17.6777 CenterY=17.6777 CenterZ=0 NormalX=0 NormalY=0 NormalZ=1 AngleXU=0 Radius=2
    g5: LineSegment [constr] StartX=0 StartY=0 StartZ=0 EndX=-17.6777 EndY=17.6777 EndZ=0
    g6: Circle CenterX=-17.6777 CenterY=-17.6777 CenterZ=0 NormalX=0 NormalY=0 NormalZ=1 AngleXU=0 Radius=2
    g7: LineSegment [constr] StartX=0 StartY=0 StartZ=0 EndX=-17.6777 EndY=-17.6777 EndZ=0
    g8: Circle CenterX=17.6777 CenterY=-17.6777 CenterZ=0 NormalX=0 NormalY=0 NormalZ=1 AngleXU=0 Radius=2
    g9: LineSegment [constr] StartX=0 StartY=0 StartZ=0 EndX=17.6777 EndY=-17.6777 EndZ=0
  constraints (24):
    c: Coincident(g0,g-1)
    c: Coincident(g1,g0)
    c: Diameter(g0) = 40
    c: Diameter(g1) = 100
    c: Diameter(g2) = 4
    c: Coincident(g3,g0)
    c: Coincident(g3,g2)
    c: Angle(g-1,g3) = 0.785398
    c: Distance(g2,g0) = 5
    c: Diameter(g4) = 4
    c: Diameter(g6) = 4
    c: Diameter(g8) = 4
    c: Coincident(g5,g4)
    c: Coincident(g7,g6)
    c: Coincident(g9,g8)
    c: Equal(g9,g3)
    c: Equal(g3,g5)
    c: Equal(g5,g7)
    c: Coincident(g5,g9)
    c: Coincident(g5,g7)
    c: Coincident(g5,g0)
    c: Perpendicular(g5,g3)
    c: Perpendicular(g5,g7)
    c: Perpendicular(g7,g9)
FEATURE [PartDesign::Pad] Pad009
  Direction = (-1,0,0)
  Length = 2
  Length2 = 10
  Placement = pos=(0,0,0) rot=(1,1,1;2.0944rad)
  Profile = -> Sketch020
  ReferenceAxis = -> Sketch020 [N_Axis]
  Refine = true
  Suppressed = false
  Type = 0
FEATURE [PartDesign::Body] Body004  label="needleGuide_baseplate"
  AllowCompound = false
  Group = -> [Sketch020,Pad009]
  Origin = -> Origin009
  Tip = -> Pad009
FEATURE [App::Part] Part001  label="Needle_guide"
  Group = -> [Body001,Body004]
  Origin = -> Origin002
FEATURE [App::Link] Needle_guide  label="Needle_guide001"
  LinkPlacement = pos=(74,-8.5e-14,-1.292e-13) rot=(1,0,0;1.27852rad)
  LinkedObject = -> Part001
  Placement = pos=(74,-8.5e-14,-1.292e-13) rot=(1,0,0;1.27852rad)
FEATURE [App::FeaturePython] Joint  label="Revolute"  # Assembly joint (typed FeaturePython)
  Activated = true
  AngleMax = 0
  AngleMin = 0
  Detach1 = false
  Detach2 = false
  Distance = 0
  Distance2 = 0
  EnableAngleMax = false
  EnableAngleMin = false
  EnableLengthMax = false
  EnableLengthMin = false
  JointType = 1 (Revolute)
  LengthMax = 0
  LengthMin = 0
  Placement1 = pos=(-72,6.26e-14,1.42e-14) rot=(0.57735,0.57735,-0.57735;4.18879rad)
  Placement2 = pos=(2,-2.13e-14,-4.7e-15) rot=(0.707107,0,0.707107;3.14159rad)
  Reference1 = -> Assembly [Needle_guide.Body004.Edge9,Needle_guide.Body004.Edge9]
  Reference2 = -> Assembly [Baseplate.Body002.Face9,Baseplate.Body002.Face9]
FEATURE [App::FeaturePython] Joint004  label="Slider"  # Assembly joint (typed FeaturePython)
  Activated = true
  AngleMax = 0
  AngleMin = 0
  Detach1 = false
  Detach2 = false
  Distance = 0
  Distance2 = 0
  EnableAngleMax = false
  EnableAngleMin = false
  EnableLengthMax = false
  EnableLengthMin = false
  JointType = 3 (Slider)
  LengthMax = 0
  LengthMin = 0
  Offset1 = pos=(0.25,0,0) rot=(0,0,1;0rad)
  Offset2 = pos=(0,0,0) rot=(0,0,-1;2.0944rad)
  Placement1 = pos=(60,-7.95,0.35) rot=(0.707107,0,0.707107;3.14159rad)
  Placement2 = pos=(6.1e-15,14.4601,-23.6457) rot=(-0.447214,-0.774597,0.447214;1.82348rad)
  Reference1 = -> Assembly [Needle.Body.Edge112,Needle.Body.Vertex73]
  Reference2 = -> Assembly [Needle_guide.Body004.Edge215,Needle_guide.Body004.Vertex149]
FEATURE [App::FeaturePython] Joint005  label="Slider001"  # Assembly joint (typed FeaturePython)
  Activated = true
  AngleMax = 0
  AngleMin = 0
  Detach1 = false
  Detach2 = false
  Distance = 0
  Distance2 = 0
  EnableAngleMax = false
  EnableAngleMin = false
  EnableLengthMax = false
  EnableLengthMin = false
  JointType = 3 (Slider)
  LengthMax = 0
  LengthMin = 0
  Offset1 = pos=(0.25,0,0) rot=(0,0,1;0rad)
  Offset2 = pos=(0,0,0) rot=(0,0,1;1.5708rad)
  Placement1 = pos=(60,-7.95,0.35) rot=(0.707107,0,0.707107;3.14159rad)
  Placement2 = pos=(-3.71e-14,-0.7,27.7078) rot=(-0.57735,0.57735,0.57735;4.18879rad)
  Reference1 = -> Assembly [Needle001.Body.Edge112,Needle001.Body.Vertex73]
  Reference2 = -> Assembly [Needle_guide.Body004.Edge131,Needle_guide.Body004.Vertex107]
FEATURE [App::FeaturePython] Joint006  label="Distance"  # Assembly joint (typed FeaturePython)
  Activated = true
  AngleMax = 0
  AngleMin = 0
  Detach1 = false
  Detach2 = false
  Distance = 0
  Distance2 = 0
  EnableAngleMax = false
  EnableAngleMin = false
  EnableLengthMax = false
  EnableLengthMin = false
  JointType = 5 (Distance)
  LengthMax = 0
  LengthMin = 0
FEATURE [Assembly::JointGroup] Joints
  Group = -> [GroundedJoint,Joint003,Joint,Joint004,Joint005,Joint006]
FEATURE [Assembly::AssemblyObject] Assembly
  Group = -> [Joints,Baseplate,GroundedJoint,Needle,Needle001,track,Joint003,Needle_guide,Joint,Joint004,Joint005,Joint006]
  Origin = -> Origin006
  Type = Assembly
